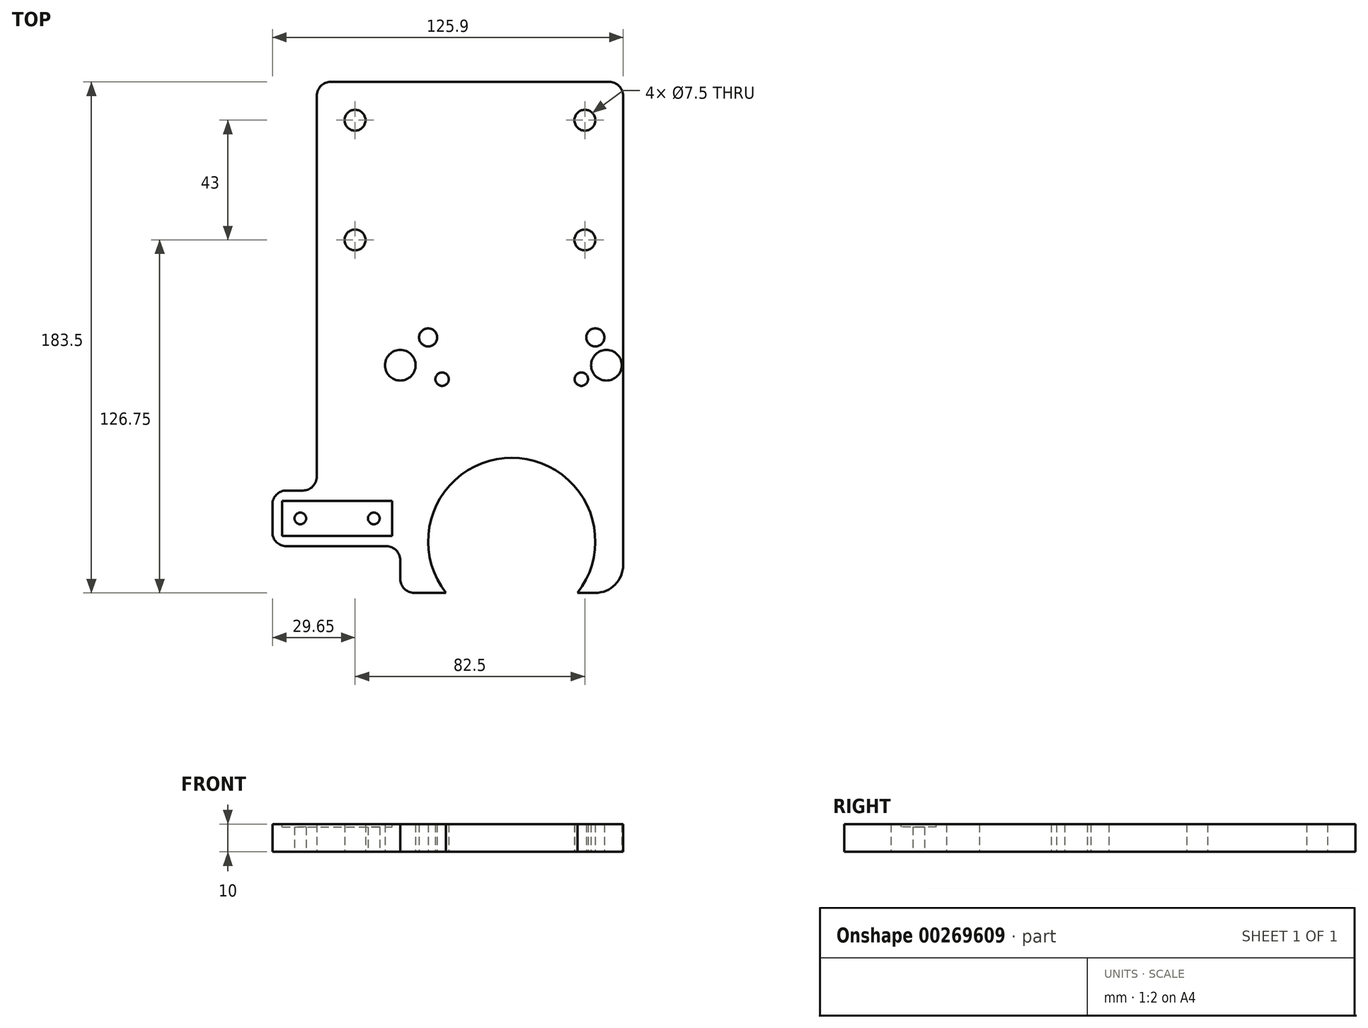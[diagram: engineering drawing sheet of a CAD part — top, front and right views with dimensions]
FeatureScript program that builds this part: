
annotation { "Feature Type Name" : "Feature", "Feature Type Description" : "" }
export const myFeature = defineFeature(function(context is Context, id is Id, definition is map)
    precondition{}
    {
        {
            var Q0;
            Q0=qCreatedBy(makeId("Top.planeOp"),FACE);
            var sketch = newSketch(context, id + "F0", { "sketchPlane" : qUnion([Q0])});
            skLineSegment(sketch, "E0.bottom", {"start": v(50, 91.75) * mm, "end": v(-50, 91.75) * mm});
            skLineSegment(sketch, "E0.left", {"start": v(55, 86.75) * mm, "end": v(55, -68.25) * mm});
            skLineSegment(sketch, "E0.right", {"start": v(-55, 86.75) * mm, "end": v(-55, -50) * mm});
            skPoint(sketch, "E0.middle", {"position": v(0, 0) * mm});
            skCircle(sketch, "E1", {"center": v(-41.25, 78) * mm, "radius": 3.75 * mm});
            skCircle(sketch, "E2", {"center": v(41.25, 78) * mm, "radius": 3.75 * mm});
            skCircle(sketch, "E3", {"center": v(41.25, 35) * mm, "radius": 3.75 * mm});
            skCircle(sketch, "E4", {"center": v(-41.25, 35) * mm, "radius": 3.75 * mm});
            skCircle(sketch, "E5", {"center": v(-34.5, -65) * mm, "radius": 2.1 * mm});
            skCircle(sketch, "E6", {"center": v(-60.9, -65) * mm, "radius": 2.1 * mm});
            skLineSegment(sketch, "E7.bottom", {"start": v(-60, -55) * mm, "end": v(-65.9, -55) * mm});
            skLineSegment(sketch, "E7.top", {"start": v(-60, -75) * mm, "end": v(-65.9, -75) * mm});
            skLineSegment(sketch, "E7.right", {"start": v(-70.9, -60) * mm, "end": v(-70.9, -70) * mm});
            skPoint(sketch, "E8.visualSharp", {"position": v(-70.9, -75) * mm});
            skArc(sketch, "E8.filletArc", {"start": v(-70.9, -70) * mm, "mid": v(-69.44, -73.54) * mm, "end": v(-65.9, -75) * mm});
            skPoint(sketch, "E9.visualSharp", {"position": v(-70.9, -55) * mm});
            skArc(sketch, "E9.filletArc", {"start": v(-65.9, -55) * mm, "mid": v(-69.44, -56.46) * mm, "end": v(-70.9, -60) * mm});
            skPoint(sketch, "E10.visualSharp", {"position": v(-55, -55) * mm});
            skArc(sketch, "E10.filletArc", {"start": v(-60, -55) * mm, "mid": v(-56.46, -53.54) * mm, "end": v(-55, -50) * mm});
            skLineSegment(sketch, "E11.top", {"start": v(45, -91.75) * mm, "end": v(38.62, -91.75) * mm});
            skLineSegment(sketch, "E11.left", {"start": v(55, -68.25) * mm, "end": v(55, -81.75) * mm});
            skArc(sketch, "E12", {"start": v(38.62, -91.75) * mm, "mid": v(15, -43.25) * mm, "end": v(-8.62, -91.75) * mm});
            skPoint(sketch, "E13.visualSharp", {"position": v(-55, 91.75) * mm});
            skArc(sketch, "E13.filletArc", {"start": v(-50, 91.75) * mm, "mid": v(-53.54, 90.29) * mm, "end": v(-55, 86.75) * mm});
            skPoint(sketch, "E14.visualSharp", {"position": v(55, 91.75) * mm});
            skArc(sketch, "E14.filletArc", {"start": v(55, 86.75) * mm, "mid": v(53.54, 90.29) * mm, "end": v(50, 91.75) * mm});
            skCircle(sketch, "E15", {"center": v(40, -15) * mm, "radius": 2.4 * mm});
            skCircle(sketch, "E16", {"center": v(-10, -15) * mm, "radius": 2.4 * mm});
            skLineSegment(sketch, "E17", {"start": v(15, -73.25) * mm, "end": v(15, -37.1) * mm, "construction": true});
            skPoint(sketch, "E18.trimOffspring.start.orphan", {"position": v(15, -15) * mm});
            skCircle(sketch, "E19", {"center": v(45, 0) * mm, "radius": 3.25 * mm});
            skCircle(sketch, "E20", {"center": v(-15, 0) * mm, "radius": 3.25 * mm});
            skCircle(sketch, "E21", {"center": v(-25, -10) * mm, "radius": 5.5 * mm});
            skCircle(sketch, "E22", {"center": v(49, -10) * mm, "radius": 5.5 * mm});
            skLineSegment(sketch, "E23", {"start": v(55, -68.25) * mm, "end": v(55, -68.25) * mm});
            skPoint(sketch, "E24.visualSharp", {"position": v(-25, -91.75) * mm});
            skLineSegment(sketch, "E24.filletArc", {"start": v(-25, -91.75) * mm, "end": v(-25, -91.75) * mm});
            skPoint(sketch, "E25.visualSharp", {"position": v(55, -91.75) * mm});
            skArc(sketch, "E25.filletArc", {"start": v(45, -91.75) * mm, "mid": v(52.07, -88.82) * mm, "end": v(55, -81.75) * mm});
            skLineSegment(sketch, "E26.trimOffspring", {"start": v(-8.62, -91.75) * mm, "end": v(-20, -91.75) * mm});
            skLineSegment(sketch, "E27", {"start": v(-60, -75) * mm, "end": v(-30, -75) * mm});
            skLineSegment(sketch, "E28", {"start": v(-25, -80) * mm, "end": v(-25, -86.75) * mm});
            skPoint(sketch, "E29.visualSharp", {"position": v(-25, -75) * mm});
            skArc(sketch, "E29.filletArc", {"start": v(-25, -80) * mm, "mid": v(-26.46, -76.46) * mm, "end": v(-30, -75) * mm});
            skArc(sketch, "E30.filletArc", {"start": v(-25, -86.75) * mm, "mid": v(-23.54, -90.29) * mm, "end": v(-20, -91.75) * mm});
            skSolve(sketch);
        }
        {
            var Q0;
            Q0 = qSketchRegion(id + "F0", true);
            extrude(context, id + "F1", {"entities" : qUnion([Q0]), "depth" : 10 * mm});
        }
        {
            var Q0;
            Q0=makeQuery(id+"F1.opExtrude","CAP_FACE",FACE,{"disambiguationData":[OSD([sQuery(id+"F0.wireOp",EDGE,"E0.bottom"),sQuery(id+"F0.wireOp",EDGE,"E0.top"),sQuery(id+"F0.wireOp",EDGE,"E0.left"),sQuery(id+"F0.wireOp",EDGE,"E0.right"),sQuery(id+"F0.wireOp",EDGE,"E1"),sQuery(id+"F0.wireOp",EDGE,"E2"),sQuery(id+"F0.wireOp",EDGE,"E3"),sQuery(id+"F0.wireOp",EDGE,"E4"),sQuery(id+"F0.wireOp",EDGE,"E5"),sQuery(id+"F0.wireOp",EDGE,"E6"),sQuery(id+"F0.wireOp",EDGE,"E7.bottom"),sQuery(id+"F0.wireOp",EDGE,"E7.top"),sQuery(id+"F0.wireOp",EDGE,"E7.right"),sQuery(id+"F0.wireOp",EDGE,"89e36223-b8c9-4d08-b781-0bd57810135a.trimOffspring"),sQuery(id+"F0.wireOp",EDGE,"c394a651-1584-4efa-b215-eac42076da8d.filletArc"),sQuery(id+"F0.wireOp",EDGE,"E8.filletArc"),sQuery(id+"F0.wireOp",EDGE,"E9.filletArc"),sQuery(id+"F0.wireOp",EDGE,"E10.filletArc"),sQuery(id+"F0.wireOp",EDGE,"E11.top"),sQuery(id+"F0.wireOp",EDGE,"E11.left"),sQuery(id+"F0.wireOp",EDGE,"E11.right"),sQuery(id+"F0.wireOp",EDGE,"dbaf0d51-8eb9-42bd-a9f4-1860f82f8f79.filletArc"),sQuery(id+"F0.wireOp",EDGE,"0a961e69-af71-4dcc-9b30-16908e0c8e77.filletArc"),sQuery(id+"F0.wireOp",EDGE,"E12"),sQuery(id+"F0.wireOp",EDGE,"E13.filletArc"),sQuery(id+"F0.wireOp",EDGE,"E14.filletArc"),sQuery(id+"F0.wireOp",EDGE,"E15"),sQuery(id+"F0.wireOp",EDGE,"E16"),sQuery(id+"F0.wireOp",EDGE,"E19"),sQuery(id+"F0.wireOp",EDGE,"E20"),sQuery(id+"F0.wireOp",EDGE,"E21"),sQuery(id+"F0.wireOp",EDGE,"E22"),sQuery(id+"F0.wireOp",EDGE,"E23"),sQuery(id+"F0.wireOp",EDGE,"E24.filletArc"),sQuery(id+"F0.wireOp",EDGE,"E25.filletArc")])],"isStart":false});
            var sketch = newSketch(context, id + "F2", { "sketchPlane" : qUnion([Q0])});
            skLineSegment(sketch, "E31.bottom", {"start": v(-67.45, -58.7) * mm, "end": v(-27.95, -58.7) * mm});
            skLineSegment(sketch, "E31.top", {"start": v(-67.45, -71.3) * mm, "end": v(-27.95, -71.3) * mm});
            skLineSegment(sketch, "E31.left", {"start": v(-67.45, -58.7) * mm, "end": v(-67.45, -71.3) * mm});
            skLineSegment(sketch, "E31.right", {"start": v(-27.95, -58.7) * mm, "end": v(-27.95, -71.3) * mm});
            skCircle(sketch, "E32", {"center": v(-60.9, -65) * mm, "radius": 2.07 * mm});
            skCircle(sketch, "E33", {"center": v(-34.5, -65) * mm, "radius": 2.04 * mm});
            skLineSegment(sketch, "E34", {"start": v(-67.45, -65) * mm, "end": v(-27.95, -65) * mm, "construction": true});
            skLineSegment(sketch, "E35", {"start": v(-47.7, -58.7) * mm, "end": v(-47.7, -71.3) * mm, "construction": true});
            skLineSegment(sketch, "E36", {"start": v(-60.9, -65) * mm, "end": v(-34.5, -65) * mm, "construction": true});
            skLineSegment(sketch, "E37", {"start": v(-47.7, -65) * mm, "end": v(-47.7, -68.03) * mm, "construction": true});
            skSolve(sketch);
        }
        {
            var Q0;
            Q0=makeQuery(id+"F2.imprint","IMPRINT",FACE,{"disambiguationData":[TD([[makeQuery(id+"F2.imprint","IMPRINT",EDGE,{"derivedFrom":sQuery(id+"F2.wireOp",EDGE,"E31.bottom")}),-1.0]])]});
            extrude(context, id + "F3", {"entities" : qUnion([Q0]), "operationType" : NewBodyOperationType.REMOVE, "oppositeDirection" : true, "depth" : 1 * mm});
        }
    });
